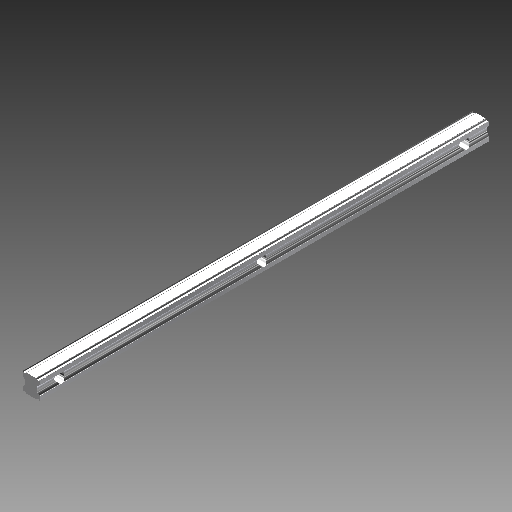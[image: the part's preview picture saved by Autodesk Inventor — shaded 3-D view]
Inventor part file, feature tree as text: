
AUTODESK INVENTOR PART (.ipt)
format: ipt  version: 2019 (Build 230136000, 136)  size: 165,376 bytes
history: native  units: mm
features: other x42, sketch x2, extrude x1, revolve x1, pattern_linear x1
ambient origin geometry x8: Origin, YZ Plane, XZ Plane, XY Plane, X Axis, Y Axis, Z Axis, Center Point
bodies: Solid1 (feature_tree)
feature tree (47):
  extrude  "Extrusion1"  TaperAngle=360.0deg  [1 undecoded]
  revolve  "Revolution1"  [1 undecoded]
  pattern_linear  "Rectangular Pattern1"  [2 undecoded]
  other  "to_ball_1_XY"
  other  "to_ball_1_YZ"
  other  "to_ball_1_ZX"
  other  "to_ball_1_X"
  other  "to_ball_1_Y"
  other  "to_ball_1_Z"
  other  "to_ball_1_Center"
  other  "to_ball_2_XY"
  other  "to_ball_2_YZ"
  other  "to_ball_2_ZX"
  other  "to_ball_2_X"
  other  "to_ball_2_Y"
  other  "to_ball_2_Z"
  other  "to_ball_2_Center"
  other  "to_ball_3_XY"
  other  "to_ball_3_YZ"
  other  "to_ball_3_ZX"
  other  "to_ball_3_X"
  other  "to_ball_3_Y"
  other  "to_ball_3_Z"
  other  "to_ball_3_Center"
  other  "to_ball_4_XY"
  other  "to_ball_4_YZ"
  other  "to_ball_4_ZX"
  other  "to_ball_4_X"
  other  "to_ball_4_Y"
  other  "to_ball_4_Z"
  other  "to_ball_4_Center"
  other  "to_body_XY"
  other  "to_body_YZ"
  other  "to_body_ZX"
  other  "to_body_X"
  other  "to_body_Y"
  other  "to_body_Z"
  other  "to_body_Center"
  other  "to_body2_XY"
  other  "to_body2_YZ"
  other  "to_body2_ZX"
  other  "to_body2_X"
  other  "to_body2_Y"
  other  "to_body2_Z"
  other  "to_body2_Center"
  sketch  "Sketch_1"  dims[d0=300.0mm d1=0.0mm d2=360.0deg]
  sketch  "Sketch_3"  dims[d3=30.0mm d5=135.0mm d6=10.0mm d8=0.0mm]
note: 4 required parameter values undecoded (feature->parameter linkage not recoverable at this tier; creation-order binding heuristic only, values carry confidence <= 0.55)
